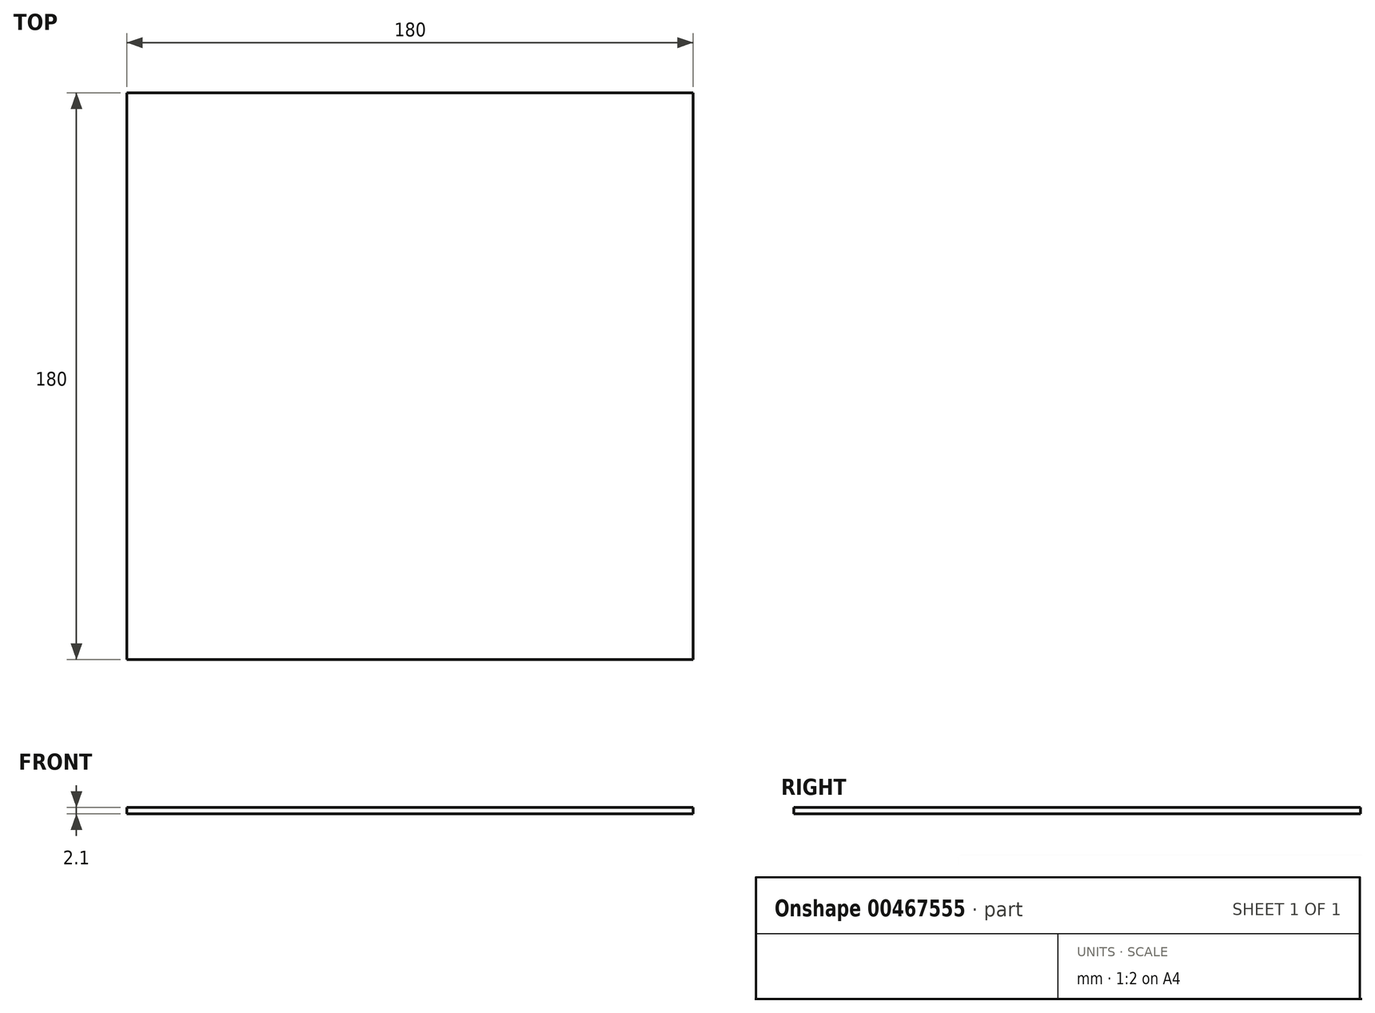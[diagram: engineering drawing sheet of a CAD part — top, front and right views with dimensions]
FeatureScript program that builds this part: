
annotation { "Feature Type Name" : "Feature", "Feature Type Description" : "" }
export const myFeature = defineFeature(function(context is Context, id is Id, definition is map)
    precondition{}
    {
        {
            var Q0;
            Q0=qCreatedBy(makeId("Top.planeOp"),FACE);
            var sketch = newSketch(context, id + "F0", { "sketchPlane" : qUnion([Q0])});
            skLineSegment(sketch, "E0.bottom", {"start": v(0, 0) * mm, "end": v(180, 0) * mm});
            skLineSegment(sketch, "E0.top", {"start": v(0, 180) * mm, "end": v(180, 180) * mm});
            skLineSegment(sketch, "E0.left", {"start": v(0, 0) * mm, "end": v(0, 180) * mm});
            skLineSegment(sketch, "E0.right", {"start": v(180, 0) * mm, "end": v(180, 180) * mm});
            skSolve(sketch);
        }
        {
            var Q0;
            Q0 = qSketchRegion(id + "F0", true);
            extrude(context, id + "F1", {"entities" : qUnion([Q0]), "depth" : 2.1 * mm});
        }
    });
